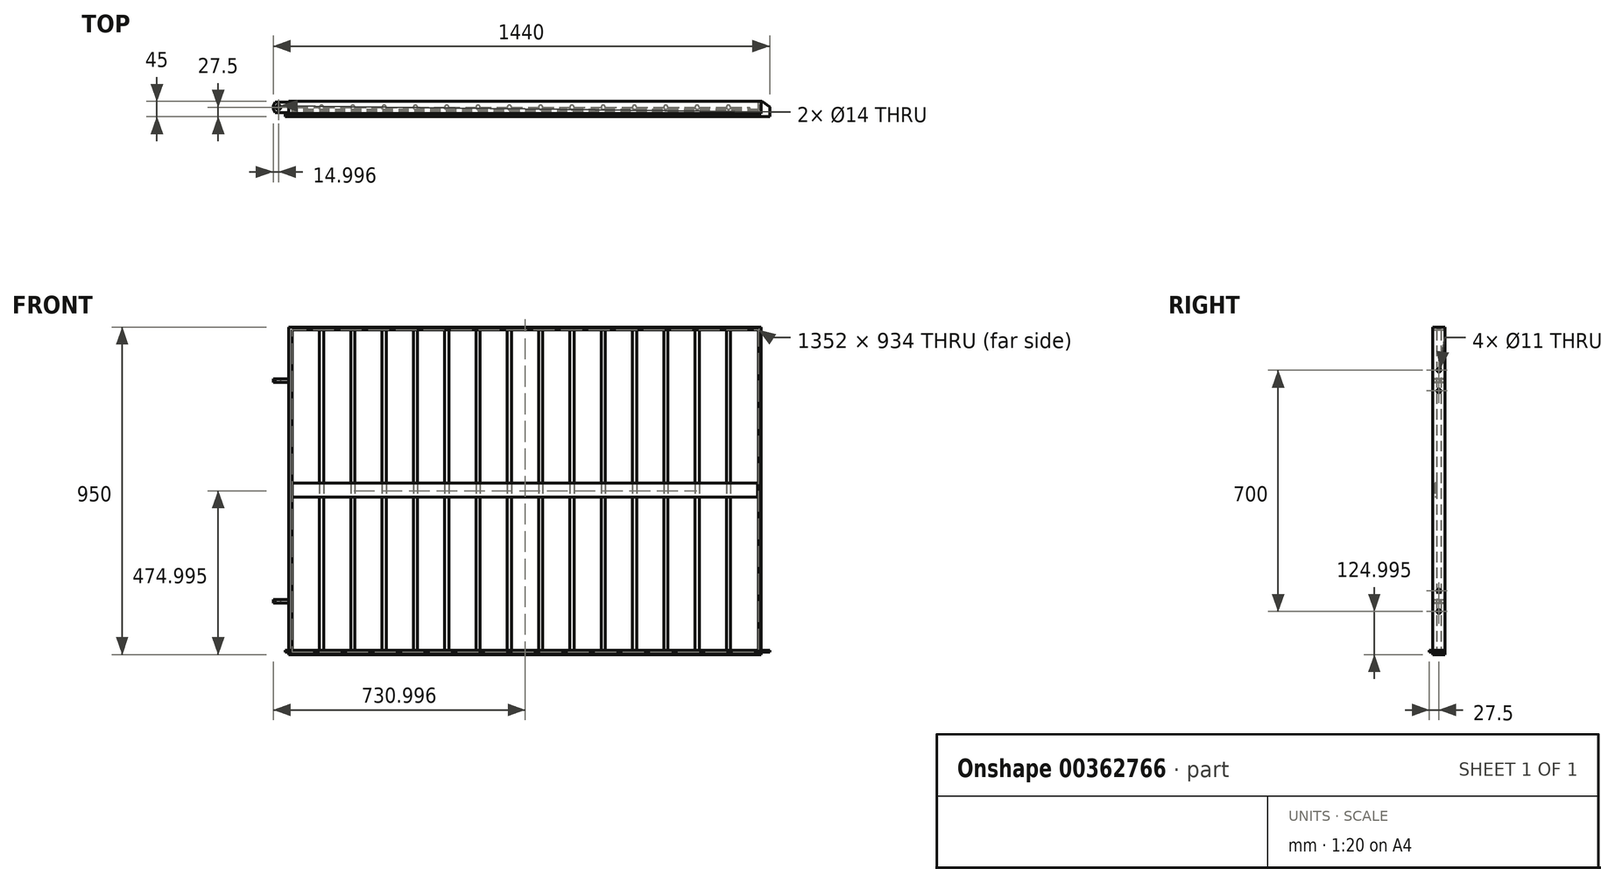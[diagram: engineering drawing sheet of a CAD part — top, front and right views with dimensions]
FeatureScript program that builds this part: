
annotation { "Feature Type Name" : "Feature", "Feature Type Description" : "" }
export const myFeature = defineFeature(function(context is Context, id is Id, definition is map)
    precondition{}
    {
        {
            var Q0;
            Q0=qCreatedBy(makeId("Front.planeOp"),FACE);
            var sketch = newSketch(context, id + "F0", { "sketchPlane" : qUnion([Q0])});
            skLineSegment(sketch, "E0.bottom", {"start": v(-700.34, 531.3) * mm, "end": v(669.66, 531.3) * mm});
            skLineSegment(sketch, "E0.top", {"start": v(-700.34, -418.7) * mm, "end": v(669.66, -418.7) * mm});
            skLineSegment(sketch, "E0.left", {"start": v(-700.34, 531.3) * mm, "end": v(-700.34, -418.7) * mm});
            skLineSegment(sketch, "E0.right", {"start": v(669.66, 531.3) * mm, "end": v(669.66, -418.7) * mm});
            skLineSegment(sketch, "E1.bottom", {"start": v(-690.34, 523.3) * mm, "end": v(669.66, 523.3) * mm});
            skLineSegment(sketch, "E1.top", {"start": v(-700.34, -410.7) * mm, "end": v(669.66, -410.7) * mm});
            skLineSegment(sketch, "E1.left", {"start": v(-690.34, 523.3) * mm, "end": v(-690.34, -410.7) * mm});
            skLineSegment(sketch, "E1.right", {"start": v(661.66, 523.3) * mm, "end": v(661.66, -410.7) * mm});
            skLineSegment(sketch, "E2.bottom", {"start": v(-609.54, 523.3) * mm, "end": v(-597.54, 523.3) * mm});
            skLineSegment(sketch, "E2.top", {"start": v(-609.54, -410.7) * mm, "end": v(-597.54, -410.7) * mm});
            skLineSegment(sketch, "E3", {"start": v(-690.34, 523.3) * mm, "end": v(-700.34, 523.3) * mm});
            skLineSegment(sketch, "E4.direction1", {"start": v(-609.54, -410.7) * mm, "end": v(-518.74, -410.7) * mm, "construction": true});
            skLineSegment(sketch, "E5", {"start": v(-700.34, -258.7) * mm, "end": v(-745.34, -258.7) * mm});
            skLineSegment(sketch, "E6", {"start": v(-745.34, -258.7) * mm, "end": v(-745.34, -268.7) * mm});
            skLineSegment(sketch, "E7", {"start": v(-745.34, -268.7) * mm, "end": v(-700.34, -268.7) * mm});
            skLineSegment(sketch, "E8", {"start": v(-700.34, 381.3) * mm, "end": v(-745.34, 381.3) * mm});
            skLineSegment(sketch, "E9", {"start": v(-745.34, 381.3) * mm, "end": v(-745.34, 371.3) * mm});
            skLineSegment(sketch, "E10", {"start": v(-745.34, 371.3) * mm, "end": v(-700.34, 371.3) * mm});
            skLineSegment(sketch, "E11.direction1", {"start": v(-603.54, -410.7) * mm, "end": v(-512.74, -410.7) * mm, "construction": true});
            skSolve(sketch);
        }
        {
            var Q0;
            {var subQ1=sQuery(id+"F0.wireOp",EDGE,"E0.bottom");Q0=makeQuery(id+"F0.imprint","IMPRINT",FACE,{"disambiguationData":[TD([[makeQuery(id+"F0.imprint","IMPRINT",EDGE,{"derivedFrom":subQ1}),-1.0]])]});}
            var Q1;
            {var subQ4=sQuery(id+"F0.wireOp",EDGE,"E0.top");Q1=makeQuery(id+"F0.imprint","IMPRINT",FACE,{"disambiguationData":[TD([[makeQuery(id+"F0.imprint","IMPRINT",EDGE,{"derivedFrom":subQ4}),1.0]])]});}
            var Q2;
            {var subQ5=sQuery(id+"F0.wireOp",EDGE,"E1.right");Q2=makeQuery(id+"F0.imprint","IMPRINT",FACE,{"disambiguationData":[TD([[makeQuery(id+"F0.imprint","IMPRINT",EDGE,{"derivedFrom":subQ5}),1.0]])]});}
            var Q3;
            {var subQ7=sQuery(id+"F0.wireOp",EDGE,"E1.left");Q3=makeQuery(id+"F0.imprint","IMPRINT",FACE,{"disambiguationData":[TD([[makeQuery(id+"F0.imprint","IMPRINT",EDGE,{"derivedFrom":subQ7}),-1.0]])]});}
            extrude(context, id + "F1", {"entities" : qUnion([Q0, Q1, Q2, Q3]), "endBound" : BoundingType.SYMMETRIC, "depth" : 35 * mm});
        }
        {
            var Q0;
            Q0=makeQuery(id+"F1.opExtrude","SWEPT_FACE",FACE,{"disambiguationData":[OSD([sQuery(id+"F0.wireOp",EDGE,"E1.top"),sQuery(id+"F0.wireOp",EDGE,"E2.top")])]});
            var sketch = newSketch(context, id + "F2", { "sketchPlane" : qUnion([Q0])});
            skCircle(sketch, "E12", {"center": v(-605.54, 0) * mm, "radius": 6 * mm});
            skCircle(sketch, "E13.1.0.0", {"center": v(-514.74, 0) * mm, "radius": 6 * mm});
            skCircle(sketch, "E13.2.0.0", {"center": v(-423.94, 0) * mm, "radius": 6 * mm});
            skCircle(sketch, "E13.3.0.0", {"center": v(-333.14, 0) * mm, "radius": 6 * mm});
            skCircle(sketch, "E13.4.0.0", {"center": v(-242.34, 0) * mm, "radius": 6 * mm});
            skCircle(sketch, "E13.5.0.0", {"center": v(-151.54, 0) * mm, "radius": 6 * mm});
            skCircle(sketch, "E13.6.0.0", {"center": v(-60.74, 0) * mm, "radius": 6 * mm});
            skCircle(sketch, "E13.7.0.0", {"center": v(30.06, 0) * mm, "radius": 6 * mm});
            skCircle(sketch, "E13.8.0.0", {"center": v(120.86, 0) * mm, "radius": 6 * mm});
            skCircle(sketch, "E13.9.0.0", {"center": v(211.66, 0) * mm, "radius": 6 * mm});
            skCircle(sketch, "E13.10.0.0", {"center": v(302.46, 0) * mm, "radius": 6 * mm});
            skCircle(sketch, "E13.11.0.0", {"center": v(393.26, 0) * mm, "radius": 6 * mm});
            skCircle(sketch, "E13.12.0.0", {"center": v(484.06, 0) * mm, "radius": 6 * mm});
            skCircle(sketch, "E13.13.0.0", {"center": v(574.86, 0) * mm, "radius": 6 * mm});
            skLineSegment(sketch, "E13.direction1", {"start": v(-605.54, 0) * mm, "end": v(-514.74, 0) * mm, "construction": true});
            skSolve(sketch);
        }
        {
            var Q0;
            Q0 = qSketchRegion(id + "F2", true);
            extrude(context, id + "F3", {"entities" : qUnion([Q0]), "operationType" : NewBodyOperationType.ADD, "depth" : 934 * mm});
        }
        {
            var Q0;
            Q0=makeQuery(id+"F1.opExtrude","SWEPT_FACE",FACE,{"disambiguationData":[OSD([sQuery(id+"F0.wireOp",EDGE,"E1.left")])]});
            var sketch = newSketch(context, id + "F4", { "sketchPlane" : qUnion([Q0])});
            skLineSegment(sketch, "E14.bottom", {"start": v(-6, 78.3) * mm, "end": v(-12, 78.3) * mm});
            skLineSegment(sketch, "E14.top", {"start": v(-6, 38.3) * mm, "end": v(-12, 38.3) * mm});
            skLineSegment(sketch, "E14.left", {"start": v(-6, 78.3) * mm, "end": v(-6, 38.3) * mm});
            skLineSegment(sketch, "E14.right", {"start": v(-12, 78.3) * mm, "end": v(-12, 38.3) * mm});
            skSolve(sketch);
        }
        {
            var Q0;
            Q0 = qSketchRegion(id + "F4", true);
            extrude(context, id + "F5", {"entities" : qUnion([Q0]), "depth" : 1350 * mm});
        }
        {
            var Q0;
            {var subQ0=sQuery(id+"F0.wireOp",EDGE,"E5");Q0=makeQuery(id+"F0.imprint","IMPRINT",FACE,{"disambiguationData":[TD([[makeQuery(id+"F0.imprint","IMPRINT",EDGE,{"derivedFrom":subQ0}),1.0]])]});}
            var Q1;
            {var subQ0=sQuery(id+"F0.wireOp",EDGE,"E8");Q1=makeQuery(id+"F0.imprint","IMPRINT",FACE,{"disambiguationData":[TD([[makeQuery(id+"F0.imprint","IMPRINT",EDGE,{"derivedFrom":subQ0}),1.0]])]});}
            extrude(context, id + "F6", {"entities" : qUnion([Q0, Q1]), "operationType" : NewBodyOperationType.ADD, "endBound" : BoundingType.SYMMETRIC, "depth" : 30 * mm});
        }
        {
            var Q0;
            Q0=makeQuery(id+"F6.opExtrude","SWEPT_FACE",FACE,{"disambiguationData":[OSD([sQuery(id+"F0.wireOp",EDGE,"E8")])]});
            var sketch = newSketch(context, id + "F7", { "sketchPlane" : qUnion([Q0])});
            skCircle(sketch, "E15", {"center": v(-730.34, 0) * mm, "radius": 7 * mm});
            skLineSegment(sketch, "E16", {"start": v(-745.34, -5) * mm, "end": v(-739.57, -15) * mm});
            skLineSegment(sketch, "E17", {"start": v(-739.57, 15) * mm, "end": v(-745.34, 5) * mm});
            skSolve(sketch);
        }
        {
            var Q0;
            Q0=makeQuery(id+"F7.imprint","IMPRINT",FACE,{"disambiguationData":[TD([[makeQuery(id+"F7.imprint","IMPRINT",EDGE,{"derivedFrom":sQuery(id+"F7.wireOp",EDGE,"E15")}),1.0]])]});
            var Q1;
            {var subQ0=sQuery(id+"F7.wireOp",EDGE,"E17");Q1=makeQuery(id+"F7.imprint","IMPRINT",FACE,{"disambiguationData":[TD([[makeQuery(id+"F7.imprint","IMPRINT",EDGE,{"derivedFrom":subQ0}),-1.0]])]});}
            var Q2;
            {var subQ0=sQuery(id+"F7.wireOp",EDGE,"E16");Q2=makeQuery(id+"F7.imprint","IMPRINT",FACE,{"disambiguationData":[TD([[makeQuery(id+"F7.imprint","IMPRINT",EDGE,{"derivedFrom":subQ0}),-1.0]])]});}
            extrude(context, id + "F8", {"entities" : qUnion([Q0, Q1, Q2]), "operationType" : NewBodyOperationType.REMOVE, "endBound" : BoundingType.THROUGH_ALL, "oppositeDirection" : true, "depth" : 25 * mm});
        }
        {
            var Q0;
            Q0=makeQuery(id+"F1.opExtrude","SWEPT_FACE",FACE,{"disambiguationData":[OSD([sQuery(id+"F0.wireOp",EDGE,"E0.right")])]});
            var sketch = newSketch(context, id + "F9", { "sketchPlane" : qUnion([Q0])});
            skCircle(sketch, "E18", {"center": v(0, 406.3) * mm, "radius": 5.5 * mm});
            skPoint(sketch, "E18.centerSnap0", {"position": v(0, 531.3) * mm});
            skCircle(sketch, "E19", {"center": v(0, 346.3) * mm, "radius": 5.5 * mm});
            skLineSegment(sketch, "E20", {"start": v(-17.5, 56.3) * mm, "end": v(17.5, 56.3) * mm});
            skCircle(sketch, "E21.MirrorC", {"center": v(0, -293.7) * mm, "radius": 5.5 * mm});
            skCircle(sketch, "E22.MirrorC", {"center": v(0, -233.7) * mm, "radius": 5.5 * mm});
            skSolve(sketch);
        }
        {
            var Q0;
            Q0 = qSketchRegion(id + "F9", true);
            extrude(context, id + "F10", {"entities" : qUnion([Q0]), "operationType" : NewBodyOperationType.REMOVE, "oppositeDirection" : true, "depth" : 10 * mm});
        }
        {
            var Q0;
            Q0=makeQuery(id+"F1.opExtrude","SWEPT_FACE",FACE,{"disambiguationData":[OSD([sQuery(id+"F0.wireOp",EDGE,"E1.top"),sQuery(id+"F0.wireOp",EDGE,"E2.top")])]});
            var sketch = newSketch(context, id + "F11", { "sketchPlane" : qUnion([Q0])});
            skLineSegment(sketch, "E23", {"start": v(-614.03, 0) * mm, "end": v(-605.54, -8.49) * mm});
            skLineSegment(sketch, "E24", {"start": v(-605.54, -8.49) * mm, "end": v(-597.06, 0) * mm});
            skLineSegment(sketch, "E25.1.0.0", {"start": v(-523.23, 0) * mm, "end": v(-514.74, -8.49) * mm});
            skLineSegment(sketch, "E25.1.0.1", {"start": v(-514.74, -8.49) * mm, "end": v(-506.26, 0) * mm});
            skLineSegment(sketch, "E25.2.0.0", {"start": v(-432.43, 0) * mm, "end": v(-423.94, -8.49) * mm});
            skLineSegment(sketch, "E25.2.0.1", {"start": v(-423.94, -8.49) * mm, "end": v(-415.46, 0) * mm});
            skLineSegment(sketch, "E25.3.0.0", {"start": v(-341.63, 0) * mm, "end": v(-333.14, -8.49) * mm});
            skLineSegment(sketch, "E25.3.0.1", {"start": v(-333.14, -8.49) * mm, "end": v(-324.66, 0) * mm});
            skLineSegment(sketch, "E25.4.0.0", {"start": v(-250.83, 0) * mm, "end": v(-242.34, -8.49) * mm});
            skLineSegment(sketch, "E25.4.0.1", {"start": v(-242.34, -8.49) * mm, "end": v(-233.86, 0) * mm});
            skLineSegment(sketch, "E25.5.0.0", {"start": v(-160.03, 0) * mm, "end": v(-151.54, -8.49) * mm});
            skLineSegment(sketch, "E25.5.0.1", {"start": v(-151.54, -8.49) * mm, "end": v(-143.06, 0) * mm});
            skLineSegment(sketch, "E25.6.0.0", {"start": v(-69.23, 0) * mm, "end": v(-60.74, -8.49) * mm});
            skLineSegment(sketch, "E25.6.0.1", {"start": v(-60.74, -8.49) * mm, "end": v(-52.26, 0) * mm});
            skLineSegment(sketch, "E25.7.0.0", {"start": v(21.57, 0) * mm, "end": v(30.06, -8.49) * mm});
            skLineSegment(sketch, "E25.7.0.1", {"start": v(30.06, -8.49) * mm, "end": v(38.54, 0) * mm});
            skLineSegment(sketch, "E25.8.0.0", {"start": v(112.37, 0) * mm, "end": v(120.86, -8.49) * mm});
            skLineSegment(sketch, "E25.8.0.1", {"start": v(120.86, -8.49) * mm, "end": v(129.34, 0) * mm});
            skLineSegment(sketch, "E25.9.0.0", {"start": v(203.17, 0) * mm, "end": v(211.66, -8.49) * mm});
            skLineSegment(sketch, "E25.9.0.1", {"start": v(211.66, -8.49) * mm, "end": v(220.14, 0) * mm});
            skLineSegment(sketch, "E25.10.0.0", {"start": v(293.97, 0) * mm, "end": v(302.46, -8.49) * mm});
            skLineSegment(sketch, "E25.10.0.1", {"start": v(302.46, -8.49) * mm, "end": v(310.94, 0) * mm});
            skLineSegment(sketch, "E25.11.0.0", {"start": v(384.77, 0) * mm, "end": v(393.26, -8.49) * mm});
            skLineSegment(sketch, "E25.11.0.1", {"start": v(393.26, -8.49) * mm, "end": v(401.74, 0) * mm});
            skLineSegment(sketch, "E25.12.0.1", {"start": v(484.06, -8.49) * mm, "end": v(492.54, 0) * mm});
            skLineSegment(sketch, "E25.direction1", {"start": v(-605.54, -8.49) * mm, "end": v(-514.74, -8.49) * mm, "construction": true});
            skLineSegment(sketch, "E26", {"start": v(-674.42, 0) * mm, "end": v(-614.03, 0) * mm});
            skLineSegment(sketch, "E27", {"start": v(661.66, -17.5) * mm, "end": v(669.66, -17.5) * mm});
            skLineSegment(sketch, "E28", {"start": v(694.66, -17.5) * mm, "end": v(694.66, -27.5) * mm});
            skLineSegment(sketch, "E29", {"start": v(694.66, -27.5) * mm, "end": v(-710.34, -27.5) * mm});
            skLineSegment(sketch, "E30", {"start": v(-710.34, -27.5) * mm, "end": v(-710.34, -17.5) * mm});
            skLineSegment(sketch, "E31", {"start": v(-710.34, -17.5) * mm, "end": v(-690.34, -17.5) * mm});
            skLineSegment(sketch, "E32", {"start": v(-690.34, -17.5) * mm, "end": v(-690.34, 0) * mm});
            skLineSegment(sketch, "E33", {"start": v(647.79, -17.5) * mm, "end": v(661.66, -17.5) * mm});
            skPoint(sketch, "E34.orphan", {"position": v(661.66, 0) * mm});
            skLineSegment(sketch, "E35.trimOffspring", {"start": v(492.54, 0) * mm, "end": v(566.37, 0) * mm});
            skLineSegment(sketch, "E36.trimOffspring", {"start": v(401.74, 0) * mm, "end": v(475.57, 0) * mm});
            skLineSegment(sketch, "E37.trimOffspring", {"start": v(-597.06, 0) * mm, "end": v(-523.23, 0) * mm});
            skLineSegment(sketch, "E38.trimOffspring", {"start": v(-506.26, 0) * mm, "end": v(-432.43, 0) * mm});
            skLineSegment(sketch, "E39.trimOffspring", {"start": v(-415.46, 0) * mm, "end": v(-341.63, 0) * mm});
            skLineSegment(sketch, "E40.trimOffspring", {"start": v(-324.66, 0) * mm, "end": v(-250.83, 0) * mm});
            skLineSegment(sketch, "E41.trimOffspring", {"start": v(-233.86, 0) * mm, "end": v(-160.03, 0) * mm});
            skLineSegment(sketch, "E42.trimOffspring", {"start": v(-143.06, 0) * mm, "end": v(-69.23, 0) * mm});
            skLineSegment(sketch, "E43.trimOffspring", {"start": v(-52.26, 0) * mm, "end": v(21.57, 0) * mm});
            skLineSegment(sketch, "E44.trimOffspring", {"start": v(38.54, 0) * mm, "end": v(112.37, 0) * mm});
            skLineSegment(sketch, "E45.trimOffspring", {"start": v(129.34, 0) * mm, "end": v(203.17, 0) * mm});
            skLineSegment(sketch, "E46.trimOffspring", {"start": v(220.14, 0) * mm, "end": v(293.97, 0) * mm});
            skLineSegment(sketch, "E47.trimOffspring", {"start": v(310.94, 0) * mm, "end": v(384.77, 0) * mm});
            skLineSegment(sketch, "E48.1.0.0", {"start": v(566.37, 0) * mm, "end": v(574.86, -8.49) * mm});
            skLineSegment(sketch, "E48.1.0.1", {"start": v(574.86, -8.49) * mm, "end": v(583.34, 0) * mm});
            skLineSegment(sketch, "E48.direction1", {"start": v(484.06, -8.49) * mm, "end": v(574.86, -8.49) * mm, "construction": true});
            skLineSegment(sketch, "E49", {"start": v(694.66, -17.5) * mm, "end": v(694.66, 0.75) * mm});
            skLineSegment(sketch, "E50", {"start": v(694.66, 0.75) * mm, "end": v(672.43, 17.5) * mm});
            skLineSegment(sketch, "E51", {"start": v(672.43, 17.5) * mm, "end": v(669.66, 17.5) * mm});
            skLineSegment(sketch, "E52", {"start": v(669.66, 17.5) * mm, "end": v(669.66, -17.5) * mm});
            skLineSegment(sketch, "E53", {"start": v(647.79, -17.5) * mm, "end": v(635.25, 0) * mm});
            skLineSegment(sketch, "E54", {"start": v(-674.42, 0) * mm, "end": v(-690.34, 17.5) * mm});
            skLineSegment(sketch, "E55", {"start": v(-690.34, 17.5) * mm, "end": v(-690.34, 0) * mm});
            skLineSegment(sketch, "E56", {"start": v(475.57, 0) * mm, "end": v(484.06, -8.49) * mm});
            skLineSegment(sketch, "E57.trimOffspring", {"start": v(583.34, 0) * mm, "end": v(635.25, 0) * mm});
            skSolve(sketch);
        }
        {
            var Q0;
            Q0 = qSketchRegion(id + "F11", true);
            extrude(context, id + "F12", {"entities" : qUnion([Q0]), "depth" : 4 * mm});
        }
        {
            var Q0;
            Q0=makeQuery(id+"F12.opExtrude","SWEPT_BODY",BODY,{"disambiguationData":[OSD([sQuery(id+"F11.wireOp",EDGE,"E23"),sQuery(id+"F11.wireOp",EDGE,"E24"),sQuery(id+"F11.wireOp",EDGE,"E25.1.0.0"),sQuery(id+"F11.wireOp",EDGE,"E25.1.0.1"),sQuery(id+"F11.wireOp",EDGE,"E25.2.0.0"),sQuery(id+"F11.wireOp",EDGE,"E25.2.0.1"),sQuery(id+"F11.wireOp",EDGE,"E25.3.0.0"),sQuery(id+"F11.wireOp",EDGE,"E25.3.0.1"),sQuery(id+"F11.wireOp",EDGE,"E25.4.0.0"),sQuery(id+"F11.wireOp",EDGE,"E25.4.0.1"),sQuery(id+"F11.wireOp",EDGE,"E25.5.0.0"),sQuery(id+"F11.wireOp",EDGE,"E25.5.0.1"),sQuery(id+"F11.wireOp",EDGE,"E25.6.0.0"),sQuery(id+"F11.wireOp",EDGE,"E25.6.0.1"),sQuery(id+"F11.wireOp",EDGE,"E25.7.0.0"),sQuery(id+"F11.wireOp",EDGE,"E25.7.0.1"),sQuery(id+"F11.wireOp",EDGE,"E25.8.0.0"),sQuery(id+"F11.wireOp",EDGE,"E25.8.0.1"),sQuery(id+"F11.wireOp",EDGE,"E25.9.0.0"),sQuery(id+"F11.wireOp",EDGE,"E25.9.0.1"),sQuery(id+"F11.wireOp",EDGE,"E25.10.0.0"),sQuery(id+"F11.wireOp",EDGE,"E25.10.0.1"),sQuery(id+"F11.wireOp",EDGE,"E25.11.0.0"),sQuery(id+"F11.wireOp",EDGE,"E25.11.0.1"),sQuery(id+"F11.wireOp",EDGE,"E25.12.0.1"),sQuery(id+"F11.wireOp",EDGE,"E26"),sQuery(id+"F11.wireOp",EDGE,"E27"),sQuery(id+"F11.wireOp",EDGE,"E28"),sQuery(id+"F11.wireOp",EDGE,"E29"),sQuery(id+"F11.wireOp",EDGE,"E30"),sQuery(id+"F11.wireOp",EDGE,"E31"),sQuery(id+"F11.wireOp",EDGE,"E32"),sQuery(id+"F11.wireOp",EDGE,"E33"),sQuery(id+"F11.wireOp",EDGE,"E35.trimOffspring"),sQuery(id+"F11.wireOp",EDGE,"E36.trimOffspring"),sQuery(id+"F11.wireOp",EDGE,"E37.trimOffspring"),sQuery(id+"F11.wireOp",EDGE,"E38.trimOffspring"),sQuery(id+"F11.wireOp",EDGE,"E39.trimOffspring"),sQuery(id+"F11.wireOp",EDGE,"E40.trimOffspring"),sQuery(id+"F11.wireOp",EDGE,"E41.trimOffspring"),sQuery(id+"F11.wireOp",EDGE,"E42.trimOffspring"),sQuery(id+"F11.wireOp",EDGE,"E43.trimOffspring"),sQuery(id+"F11.wireOp",EDGE,"E44.trimOffspring"),sQuery(id+"F11.wireOp",EDGE,"E45.trimOffspring"),sQuery(id+"F11.wireOp",EDGE,"E46.trimOffspring"),sQuery(id+"F11.wireOp",EDGE,"E47.trimOffspring"),sQuery(id+"F11.wireOp",EDGE,"E48.1.0.0"),sQuery(id+"F11.wireOp",EDGE,"E48.1.0.1"),sQuery(id+"F11.wireOp",EDGE,"E49"),sQuery(id+"F11.wireOp",EDGE,"E50"),sQuery(id+"F11.wireOp",EDGE,"E51"),sQuery(id+"F11.wireOp",EDGE,"E52"),sQuery(id+"F11.wireOp",EDGE,"E53"),sQuery(id+"F11.wireOp",EDGE,"E54"),sQuery(id+"F11.wireOp",EDGE,"E55"),sQuery(id+"F11.wireOp",EDGE,"E56"),sQuery(id+"F11.wireOp",EDGE,"E57.trimOffspring")])]});
            transform(context, id + "F13", {"entities" : qUnion([Q0]), "transformType" : TransformType.TRANSLATION_3D, "dx" : 0 * mm, "dy" : 0 * mm, "dz" : 0 * mm, "makeCopy" : true});
        }
        {
            var Q0;
            Q0=makeQuery(id+"F13.opPattern","COPY",BODY,{"derivedFrom":makeQuery(id+"F12.opExtrude","SWEPT_BODY",BODY,{"disambiguationData":[OSD([sQuery(id+"F11.wireOp",EDGE,"E23"),sQuery(id+"F11.wireOp",EDGE,"E24"),sQuery(id+"F11.wireOp",EDGE,"E25.1.0.0"),sQuery(id+"F11.wireOp",EDGE,"E25.1.0.1"),sQuery(id+"F11.wireOp",EDGE,"E25.2.0.0"),sQuery(id+"F11.wireOp",EDGE,"E25.2.0.1"),sQuery(id+"F11.wireOp",EDGE,"E25.3.0.0"),sQuery(id+"F11.wireOp",EDGE,"E25.3.0.1"),sQuery(id+"F11.wireOp",EDGE,"E25.4.0.0"),sQuery(id+"F11.wireOp",EDGE,"E25.4.0.1"),sQuery(id+"F11.wireOp",EDGE,"E25.5.0.0"),sQuery(id+"F11.wireOp",EDGE,"E25.5.0.1"),sQuery(id+"F11.wireOp",EDGE,"E25.6.0.0"),sQuery(id+"F11.wireOp",EDGE,"E25.6.0.1"),sQuery(id+"F11.wireOp",EDGE,"E25.7.0.0"),sQuery(id+"F11.wireOp",EDGE,"E25.7.0.1"),sQuery(id+"F11.wireOp",EDGE,"E25.8.0.0"),sQuery(id+"F11.wireOp",EDGE,"E25.8.0.1"),sQuery(id+"F11.wireOp",EDGE,"E25.9.0.0"),sQuery(id+"F11.wireOp",EDGE,"E25.9.0.1"),sQuery(id+"F11.wireOp",EDGE,"E25.10.0.0"),sQuery(id+"F11.wireOp",EDGE,"E25.10.0.1"),sQuery(id+"F11.wireOp",EDGE,"E25.11.0.0"),sQuery(id+"F11.wireOp",EDGE,"E25.11.0.1"),sQuery(id+"F11.wireOp",EDGE,"E25.12.0.1"),sQuery(id+"F11.wireOp",EDGE,"E26"),sQuery(id+"F11.wireOp",EDGE,"E27"),sQuery(id+"F11.wireOp",EDGE,"E28"),sQuery(id+"F11.wireOp",EDGE,"E29"),sQuery(id+"F11.wireOp",EDGE,"E30"),sQuery(id+"F11.wireOp",EDGE,"E31"),sQuery(id+"F11.wireOp",EDGE,"E32"),sQuery(id+"F11.wireOp",EDGE,"E33"),sQuery(id+"F11.wireOp",EDGE,"E35.trimOffspring"),sQuery(id+"F11.wireOp",EDGE,"E36.trimOffspring"),sQuery(id+"F11.wireOp",EDGE,"E37.trimOffspring"),sQuery(id+"F11.wireOp",EDGE,"E38.trimOffspring"),sQuery(id+"F11.wireOp",EDGE,"E39.trimOffspring"),sQuery(id+"F11.wireOp",EDGE,"E40.trimOffspring"),sQuery(id+"F11.wireOp",EDGE,"E41.trimOffspring"),sQuery(id+"F11.wireOp",EDGE,"E42.trimOffspring"),sQuery(id+"F11.wireOp",EDGE,"E43.trimOffspring"),sQuery(id+"F11.wireOp",EDGE,"E44.trimOffspring"),sQuery(id+"F11.wireOp",EDGE,"E45.trimOffspring"),sQuery(id+"F11.wireOp",EDGE,"E46.trimOffspring"),sQuery(id+"F11.wireOp",EDGE,"E47.trimOffspring"),sQuery(id+"F11.wireOp",EDGE,"E48.1.0.0"),sQuery(id+"F11.wireOp",EDGE,"E48.1.0.1"),sQuery(id+"F11.wireOp",EDGE,"E49"),sQuery(id+"F11.wireOp",EDGE,"E50"),sQuery(id+"F11.wireOp",EDGE,"E51"),sQuery(id+"F11.wireOp",EDGE,"E52"),sQuery(id+"F11.wireOp",EDGE,"E53"),sQuery(id+"F11.wireOp",EDGE,"E54"),sQuery(id+"F11.wireOp",EDGE,"E55"),sQuery(id+"F11.wireOp",EDGE,"E56"),sQuery(id+"F11.wireOp",EDGE,"E57.trimOffspring")])]}),"instanceName":"1"});
            deleteBodies(context, id + "F14", {"entities" : qUnion([Q0])});
        }
    });
